annotation { "Feature Type Name" : "Feature", "Feature Type Description" : "" }
export const myFeature = defineFeature(function(context is Context, id is Id, definition is map)
    precondition{}
    {
        {
            var Q0;
            Q0=qCreatedBy(makeId("Front.planeOp"),FACE);
            var sketch = newSketch(context, id + "F0", { "sketchPlane" : qUnion([Q0])});
            skCircle(sketch, "E0", {"center": v(-96.31, 66.5) * mm, "radius": 9.53 * mm});
            skLineSegment(sketch, "E1", {"start": v(-96.31, 66.5) * mm, "end": v(-96.31, -47.8) * mm});
            skPoint(sketch, "E2.start.orphan", {"position": v(-271.1, -47.8) * mm});
            skCircle(sketch, "E3", {"center": v(-96.31, 15.7) * mm, "radius": 15.88 * mm});
            skCircle(sketch, "E4", {"center": v(-96.31, -47.8) * mm, "radius": 9.53 * mm});
            skLineSegment(sketch, "E5", {"start": v(-96.31, -47.8) * mm, "end": v(-51.86, -47.8) * mm});
            skCircle(sketch, "E6", {"center": v(-51.86, -47.8) * mm, "radius": 7.94 * mm});
            skLineSegment(sketch, "E7", {"start": v(-96.31, 15.7) * mm, "end": v(-96.31, -47.8) * mm});
            skLineSegment(sketch, "E8", {"start": v(-105.76, 67.7) * mm, "end": v(-112.06, 17.69) * mm});
            skLineSegment(sketch, "E9", {"start": v(-86.86, 67.7) * mm, "end": v(-80.56, 17.69) * mm});
            skCircle(sketch, "E10", {"center": v(-99.58, 52.23) * mm, "radius": 1.59 * mm});
            skCircle(sketch, "E11", {"center": v(-96.31, 66.5) * mm, "radius": 3.18 * mm});
            skCircle(sketch, "E12", {"center": v(-96.31, 15.7) * mm, "radius": 3.18 * mm});
            skCircle(sketch, "E13", {"center": v(-96.31, -47.8) * mm, "radius": 3.18 * mm});
            skCircle(sketch, "E14", {"center": v(-51.86, -47.8) * mm, "radius": 3.18 * mm});
            skLineSegment(sketch, "E15", {"start": v(-96.31, 15.7) * mm, "end": v(-96.31, 52.23) * mm});
            skLineSegment(sketch, "E16", {"start": v(-80.52, 14.11) * mm, "end": v(-84.97, -30.2) * mm});
            skLineSegment(sketch, "E17", {"start": v(-112.1, 14.11) * mm, "end": v(-105.8, -48.75) * mm});
            skLineSegment(sketch, "E18", {"start": v(-77.35, -38.94) * mm, "end": v(-51.58, -39.87) * mm});
            skLineSegment(sketch, "E19", {"start": v(-95.97, -57.32) * mm, "end": v(-51.58, -55.73) * mm});
            skArc(sketch, "E20.filletArc", {"start": v(-84.97, -30.2) * mm, "mid": v(-83.05, -36.23) * mm, "end": v(-77.35, -38.94) * mm});
            skText(sketch, "E21", { "text": "5.887 in^3", "fontName": "OpenSans-Regular.ttf"});
            skText(sketch, "E22", { "text": "Christian Smith", "fontName": "OpenSans-Bold.ttf"});
            const initialGuessF0  = {"E21": [-0.1382, -0.08287, 1, 0, 0.01564], "E22": [-0.331, -0.0852, 1, 0, 0.01796]};
            skSetInitialGuess(sketch, initialGuessF0);
            skSolve(sketch);
        }
        {
            var Q0;
            Q0 = qSketchRegion(id + "F0", true);
            var Q1;
            {var subQ0=sQuery(id+"F0.wireOp",EDGE,"E7");var subQ1=sQuery(id+"F0.wireOp",EDGE,"E4");var subQ2=makeQuery(id+"F0.imprint","INTERSECT",VERTEX,{"derivedFrom":[subQ1,subQ0]});Q1=makeQuery(id+"F0.imprint","IMPRINT",FACE,{"disambiguationData":[TD([[makeQuery(id+"F0.imprint","IMPRINT",EDGE,{"disambiguationData":[TD([[subQ2,1.0]])],"derivedFrom":subQ1}),1.0]])]});}
            extrude(context, id + "F1", {"entities" : qUnion([Q0, Q1]), "depth" : 25.4 * mm, "offsetDistance" : 25.4 * mm});
        }
    });